# Revit family: Gira_5051028
name_source: partatom
category: Elektroinstallationen
revit_build: Autodesk Revit 2017 (Build: 20160225_1515(x64)
units: mm (PartAtom-declared; Revit-internal decimal feet)

## family parameters
Basisbauteil = Fläche
Beim Laden mit Abzugskörper schneiden = Nein
Bemaßung runder Anschluss = Durchmesser verwenden
Beschriftungsausrichtung beibehalten = Nein
Gemeinsam genutzt = Nein
Raumberechnungspunkt = Nein
Teiletyp = Normal

## types (1)
- Tastsens.4 24 V 1f TS4 Anthrazit
    Andere Bussysteme = ohne
    Anzahl der Betätigungspunkte = 2
    Anzahl der Tasten = 1
    BIM = https://media.stage.bim.site TS4 1fach.rfa
    BIMSITE_PRODUCT_ID = 8fc481d81ca8bcf9651317b8a25061c75db55e9c
    Beschreibung = Tastsensor 4 24 V 1fach  Anthrazit Merkmale:  Tastsensor 4 zum Anschluss an 24 V Steuersysteme.  Zwei weiße Status-LEDs pro Wippe.  Messung der Raumtemperatur mit integriertem Temperatursensor (PT1000).  Hinweise :  Nur für SELV-Stromkreise geeignet.  Professionelle Beschriftung über den Gira Beschriftungsservice www.beschriftung.gira.de.  Der Tastsensor wird mit einer programmneutralen Inbetriebnahme-Wippe geliefert. Das passende Wippenset zum Schalterprogramm ist separat zu bestellen.
    Bussystem Funkbus = Nein
    Bussystem KNX = Ja
    Bussystem KNX-Funk = Nein
    Bussystem LON = Nein
    Bussystem Powernet = Nein
    Datenblatt = https://media.stage.bim.site
    Farbe = anthrazit
    Funk bidirektional = Nein
    GTIN = 4010337074977
    HAN = 5051028
    HeinzeBIM = https://www.heinze.de
    Hersteller = Gira
    Kosten = 0 $
    Mit Beschriftungsfeld = Nein
    Mit Busankopplung = Nein
    Mit Diebstahl-/Demontageschutz = Ja
    Mit Display = Nein
    Mit Infrarotsensor = Nein
    Mit LED-Anzeige = Ja
    Mit Raumthermostat = Nein
    Montageart = Unterputz
    Oberfläche Text = sonstige
    Produktseite = https://media.stage.bim.site
    Schutzart (IP) = IP20
    Transparent = Nein
    Typname = Tastsens.4 24 V 1f TS4 Anthrazit
    URL = https://www.gira.de
    Vorgabe-Ansicht = 1219 mm
    Werkstoff Text = sonstige
    Werkstoffgüte = sonstige
    White = White

## geometry (parser evidence)
native form markers: Sweep x3
no freeform markers — native parametric forms only
